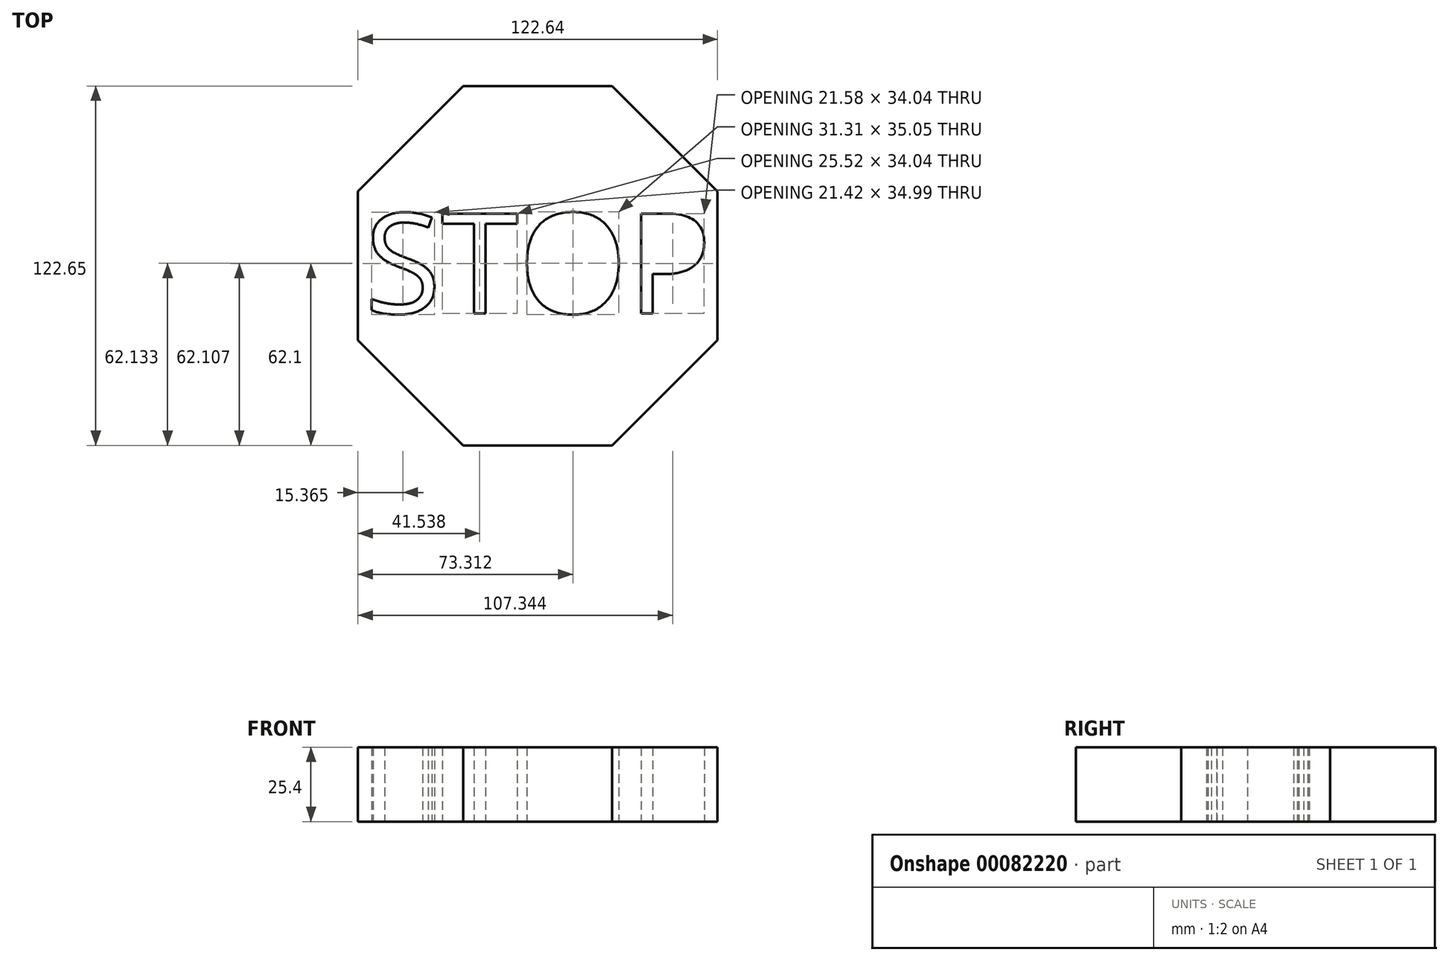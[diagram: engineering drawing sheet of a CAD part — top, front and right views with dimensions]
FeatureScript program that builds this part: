
annotation { "Feature Type Name" : "Feature", "Feature Type Description" : "" }
export const myFeature = defineFeature(function(context is Context, id is Id, definition is map)
    precondition{}
    {
        {
            var Q0;
            Q0=qCreatedBy(makeId("Top.planeOp"),FACE);
            var sketch = newSketch(context, id + "F0", { "sketchPlane" : qUnion([Q0])});
            skCircle(sketch, "E0.cCircle", {"center": v(0, 23.6) * mm, "radius": 61.32 * mm, "construction": true});
            skLineSegment(sketch, "E0.0", {"start": v(25.4, -37.72) * mm, "end": v(-25.4, -37.72) * mm});
            skLineSegment(sketch, "E0.1", {"start": v(-25.4, -37.72) * mm, "end": v(-61.32, -1.8) * mm});
            skLineSegment(sketch, "E0.2", {"start": v(-61.32, -1.8) * mm, "end": v(-61.32, 49) * mm});
            skLineSegment(sketch, "E0.3", {"start": v(-61.32, 49) * mm, "end": v(-25.4, 84.93) * mm});
            skLineSegment(sketch, "E0.4", {"start": v(-25.4, 84.93) * mm, "end": v(25.4, 84.93) * mm});
            skLineSegment(sketch, "E0.5", {"start": v(25.4, 84.93) * mm, "end": v(61.32, 49) * mm});
            skLineSegment(sketch, "E0.6", {"start": v(61.32, 49) * mm, "end": v(61.32, -1.8) * mm});
            skLineSegment(sketch, "E0.7", {"start": v(61.32, -1.8) * mm, "end": v(25.4, -37.72) * mm});
            skPoint(sketch, "E0.0.midPoint", {"position": v(0, -37.72) * mm});
            skText(sketch, "E1", { "text": "STOP", "fontName": "OpenSans-Regular.ttf"});
            const initialGuessF0  = {"E1": [-0.05913, 0.00736, 1, 0, 0.03433]};
            skSetInitialGuess(sketch, initialGuessF0);
            skSolve(sketch);
        }
        {
            var Q0;
            Q0 = qSketchRegion(id + "F0", true);
            extrude(context, id + "F1", {"entities" : qUnion([Q0]), "depth" : 25.4 * mm});
        }
    });
